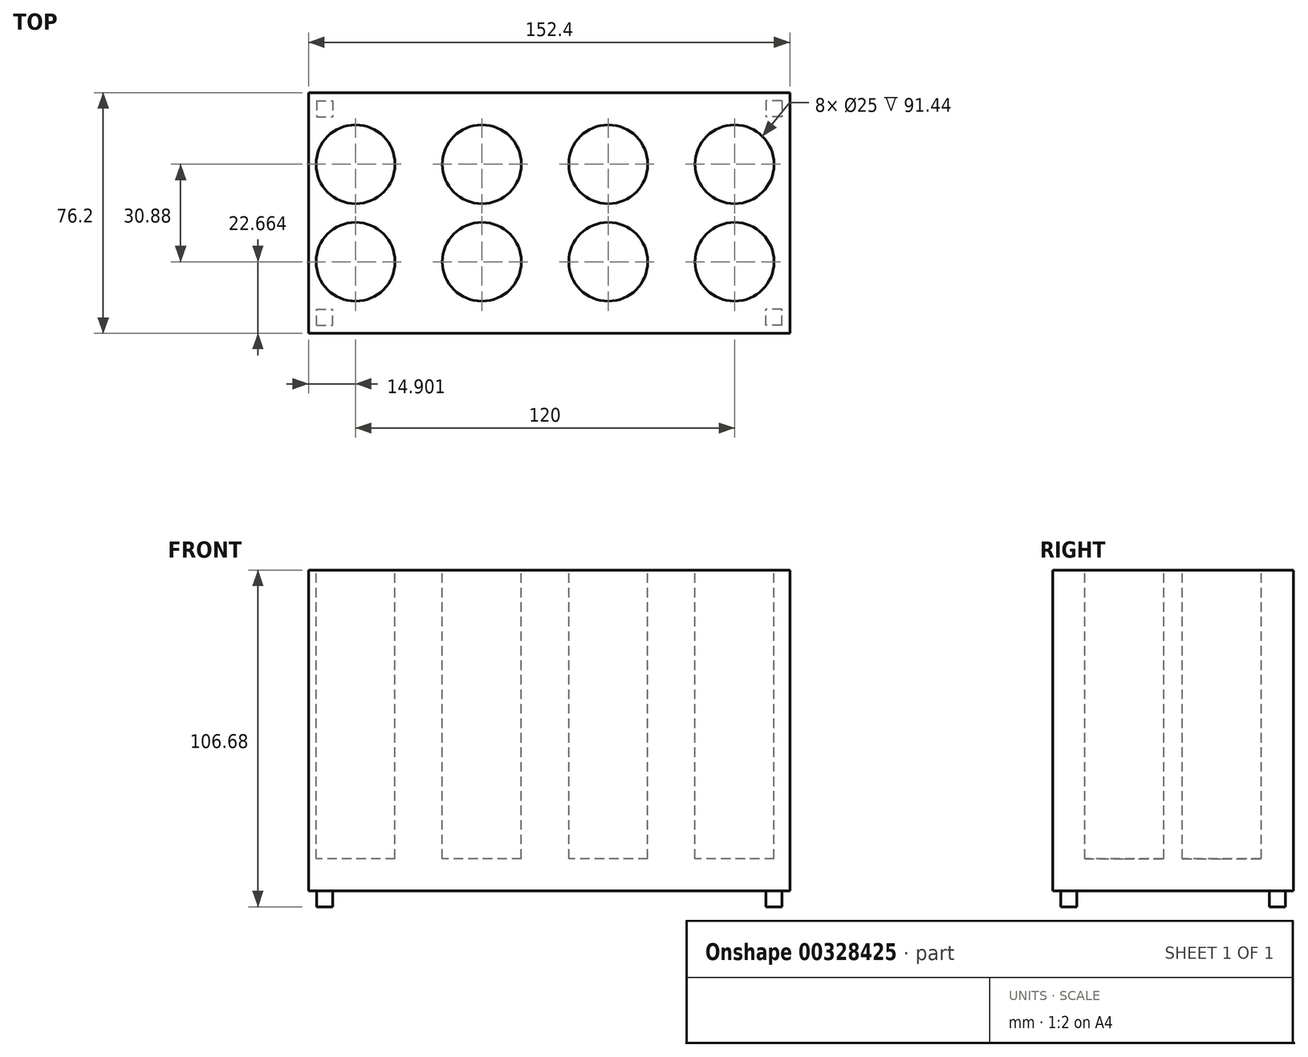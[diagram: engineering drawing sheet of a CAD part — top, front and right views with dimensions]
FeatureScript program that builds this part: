
annotation { "Feature Type Name" : "Feature", "Feature Type Description" : "" }
export const myFeature = defineFeature(function(context is Context, id is Id, definition is map)
    precondition{}
    {
        {
            var Q0;
            Q0=qCreatedBy(makeId("Top.planeOp"),FACE);
            var sketch = newSketch(context, id + "F0", { "sketchPlane" : qUnion([Q0])});
            skLineSegment(sketch, "E0.bottom", {"start": v(-408.6, 42.01) * mm, "end": v(-256.2, 42.01) * mm});
            skLineSegment(sketch, "E0.top", {"start": v(-408.6, -34.19) * mm, "end": v(-256.2, -34.19) * mm});
            skLineSegment(sketch, "E0.left", {"start": v(-408.6, 42.01) * mm, "end": v(-408.6, -34.19) * mm});
            skLineSegment(sketch, "E0.right", {"start": v(-256.2, 42.01) * mm, "end": v(-256.2, -34.19) * mm});
            skSolve(sketch);
        }
        {
            var Q0;
            Q0 = qSketchRegion(id + "F0", true);
            extrude(context, id + "F1", {"entities" : qUnion([Q0]), "depth" : 101.6 * mm});
        }
        {
            var Q0;
            Q0=makeQuery(id+"F1.opExtrude","CAP_FACE",FACE,{"disambiguationData":[OSD([sQuery(id+"F0.wireOp",EDGE,"E0.bottom"),sQuery(id+"F0.wireOp",EDGE,"E0.top"),sQuery(id+"F0.wireOp",EDGE,"E0.left"),sQuery(id+"F0.wireOp",EDGE,"E0.right")])],"isStart":false});
            var sketch = newSketch(context, id + "F2", { "sketchPlane" : qUnion([Q0])});
            skCircle(sketch, "E1", {"center": v(-393.7, 19.35) * mm, "radius": 12.5 * mm});
            skCircle(sketch, "E2", {"center": v(-353.7, 19.35) * mm, "radius": 12.5 * mm});
            skCircle(sketch, "E3", {"center": v(-313.7, 19.35) * mm, "radius": 12.5 * mm});
            skCircle(sketch, "E4", {"center": v(-273.7, -11.53) * mm, "radius": 12.5 * mm});
            skCircle(sketch, "E5", {"center": v(-313.7, -11.53) * mm, "radius": 12.5 * mm});
            skCircle(sketch, "E6", {"center": v(-353.7, -11.53) * mm, "radius": 12.5 * mm});
            skCircle(sketch, "E7", {"center": v(-393.7, -11.53) * mm, "radius": 12.5 * mm});
            skCircle(sketch, "E8", {"center": v(-273.7, 19.35) * mm, "radius": 12.5 * mm});
            skSolve(sketch);
        }
        {
            var Q0;
            Q0 = qSketchRegion(id + "F2", true);
            extrude(context, id + "F3", {"entities" : qUnion([Q0]), "operationType" : NewBodyOperationType.REMOVE, "oppositeDirection" : true, "depth" : 91.44 * mm});
        }
        {
            var Q0;
            Q0=makeQuery(id+"F1.opExtrude","CAP_FACE",FACE,{"disambiguationData":[OSD([sQuery(id+"F0.wireOp",EDGE,"E0.bottom"),sQuery(id+"F0.wireOp",EDGE,"E0.top"),sQuery(id+"F0.wireOp",EDGE,"E0.left"),sQuery(id+"F0.wireOp",EDGE,"E0.right")])],"isStart":true});
            var sketch = newSketch(context, id + "F4", { "sketchPlane" : qUnion([Q0])});
            skLineSegment(sketch, "E9.bottom", {"start": v(-406.06, 31.65) * mm, "end": v(-400.98, 31.65) * mm});
            skLineSegment(sketch, "E9.top", {"start": v(-406.06, 26.57) * mm, "end": v(-400.98, 26.57) * mm});
            skLineSegment(sketch, "E9.left", {"start": v(-406.06, 31.65) * mm, "end": v(-406.06, 26.57) * mm});
            skLineSegment(sketch, "E9.right", {"start": v(-400.98, 31.65) * mm, "end": v(-400.98, 26.57) * mm});
            skLineSegment(sketch, "E10.bottom", {"start": v(-406.06, -39.47) * mm, "end": v(-400.98, -39.47) * mm});
            skLineSegment(sketch, "E10.top", {"start": v(-406.06, -34.4) * mm, "end": v(-400.98, -34.4) * mm});
            skLineSegment(sketch, "E10.left", {"start": v(-406.06, -39.47) * mm, "end": v(-406.06, -34.4) * mm});
            skLineSegment(sketch, "E10.right", {"start": v(-400.98, -39.47) * mm, "end": v(-400.98, -34.4) * mm});
            skLineSegment(sketch, "E11.bottom", {"start": v(-258.74, -39.47) * mm, "end": v(-263.82, -39.47) * mm});
            skLineSegment(sketch, "E11.top", {"start": v(-258.74, -34.4) * mm, "end": v(-263.82, -34.4) * mm});
            skLineSegment(sketch, "E11.left", {"start": v(-258.74, -39.47) * mm, "end": v(-258.74, -34.4) * mm});
            skLineSegment(sketch, "E11.right", {"start": v(-263.82, -39.47) * mm, "end": v(-263.82, -34.4) * mm});
            skLineSegment(sketch, "E12.bottom", {"start": v(-258.74, 31.65) * mm, "end": v(-263.82, 31.65) * mm});
            skLineSegment(sketch, "E12.top", {"start": v(-258.74, 26.57) * mm, "end": v(-263.82, 26.57) * mm});
            skLineSegment(sketch, "E12.left", {"start": v(-258.74, 31.65) * mm, "end": v(-258.74, 26.57) * mm});
            skLineSegment(sketch, "E12.right", {"start": v(-263.82, 31.65) * mm, "end": v(-263.82, 26.57) * mm});
            skSolve(sketch);
        }
        {
            var Q0;
            Q0 = qSketchRegion(id + "F4", true);
            extrude(context, id + "F5", {"entities" : qUnion([Q0]), "operationType" : NewBodyOperationType.ADD, "depth" : 5.08 * mm});
        }
    });
